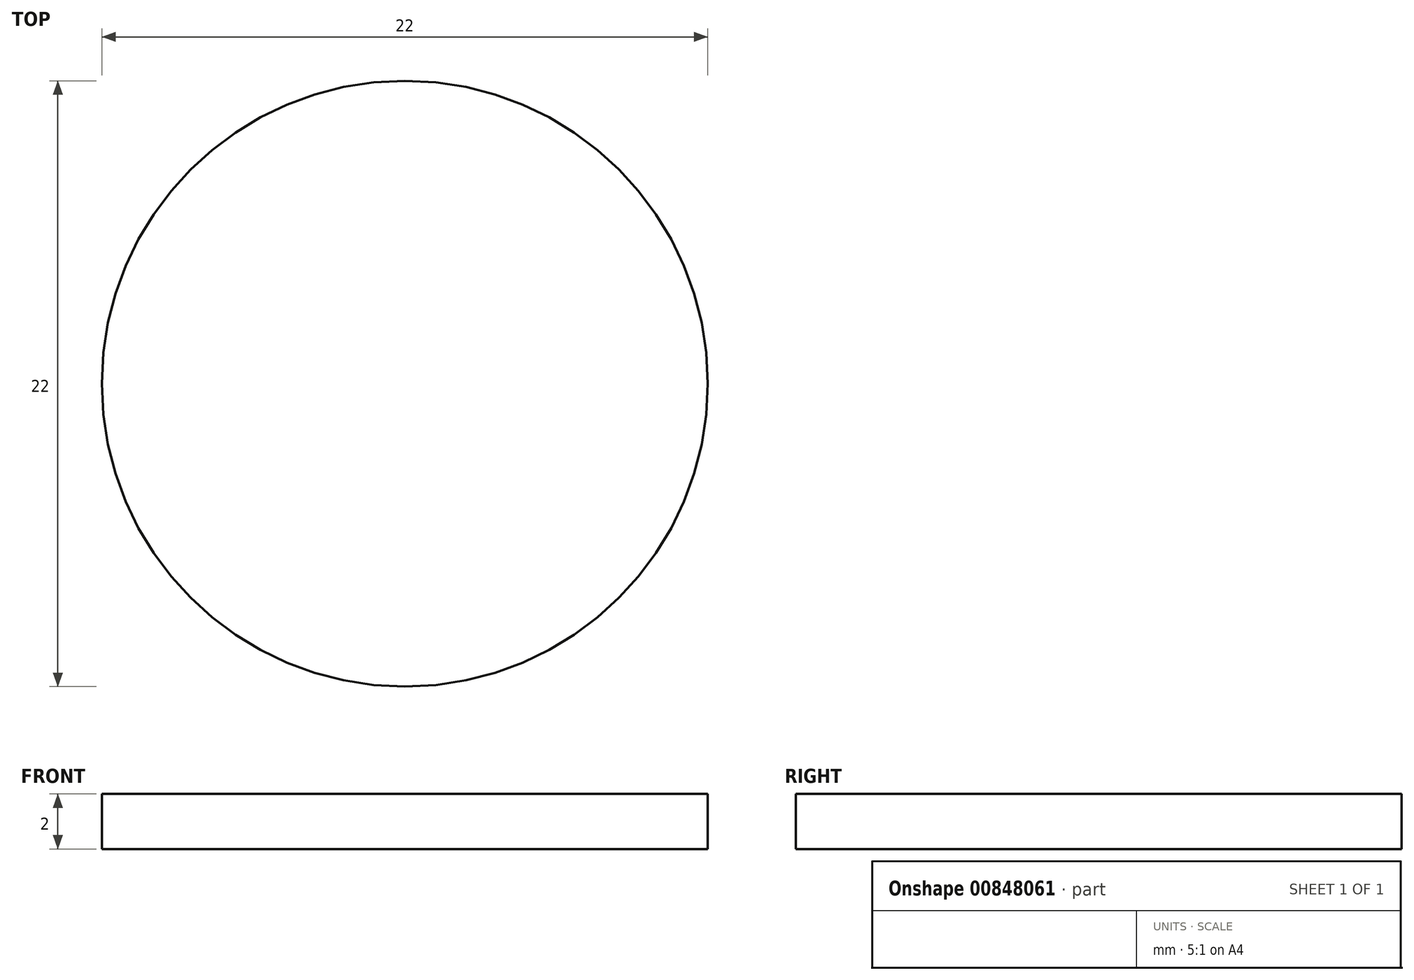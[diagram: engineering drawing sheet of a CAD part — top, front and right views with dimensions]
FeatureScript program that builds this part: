
annotation { "Feature Type Name" : "Feature", "Feature Type Description" : "" }
export const myFeature = defineFeature(function(context is Context, id is Id, definition is map)
    precondition{}
    {
        {
            var Q0;
            Q0=qCreatedBy(makeId("Top.planeOp"),FACE);
            var sketch = newSketch(context, id + "F0", { "sketchPlane" : qUnion([Q0])});
            skCircle(sketch, "E0", {"center": v(0, 0) * mm, "radius": 11 * mm});
            skSolve(sketch);
        }
        {
            var Q0;
            Q0 = qSketchRegion(id + "F0", true);
            extrude(context, id + "F1", {"entities" : qUnion([Q0]), "depth" : 2 * mm, "offsetDistance" : 25 * mm});
        }
    });
